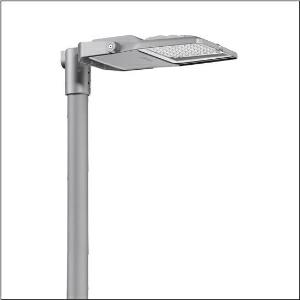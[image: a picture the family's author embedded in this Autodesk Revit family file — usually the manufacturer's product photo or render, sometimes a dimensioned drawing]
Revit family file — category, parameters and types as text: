
# Revit family: floodlight_fl_21_mini___pl43_5xa7776d2a3a_6ee6
name_source: partatom
category: Lighting Fixtures
units: mm (PartAtom-declared; Revit-internal decimal feet)

## family parameters
Cut with Voids When Loaded = No
Host = Face
Light Source = No
Part Type = Normal
Room Calculation Point = No
Round Connector Dimension = Use Diameter
Shared = No

## types (1)
- --- (1 x LED, 18300 lm, 142.9 W, 3000K)
    Apparent Load = 143 VA
    CIE Flux Codes = 27 78 99 100 100
    Color Rendering = 70
    Color Temperature = 3000K
    Default Elevation = 1800 mm
    Description = Floodlight FL 21 mini, floodlight, primary light control with lens, of PMMA, primary optical cover: protective disc, of toughened safety glass, transparent, light distribution: PL43, light emission: direct distribution, installation type: surface-mounted, LED, High Power LED, rated luminous flux: 18.300lm, luminous efficacy: 128lm/W, light colour: 730, colour temperature: 3000K, control: flexible luminous flux parameterisation, time-dependent luminous flux control, constant luminous flux control, overheat protection, pre-setting: logarithmic dimming characteristic, with terminal, 6-pole, mains connection: 220..240V, AC, 50/60Hz, start of lifetime: 143W, end of service life: 151W, reduction: 63W, luminaire housing, of diecast aluminium, powder-coated, Siteco® metallic grey (DB 702S), corrosivity category C5 mid according to DIN EN ISO 12944, sealing non-destructively replaceable, please order mast flange separately, mast bracket, of steel, galvanised, powder-coated, Siteco® metallic grey (DB 702S), Smart Interface below and above, protection rating (complete): IP66, insulation class (complete): insulation class II (safety insulation), certification: CE, ENEC, VDE, protection symbol: D, impact resistance: IK08, permissible operating ambient temperature: -40..+40°C, permissible operating ambient temperature for outdoor applications: -40..+50°C, standard: DIN EN 12944, LABS conformity tested according to VDMA 24364:2018-05, packaging unit: 1 piece

Light Distribution: PL43
    Height = 70 mm
    Lamp = 1 x LED
    Lamp Light Flux = 18300 lm
    Lamp Power = 142.9 W
    Lamp count = 1
    Length = 485 mm
    Luminous efficacy = 128 lm/W
    Manufacturer = Siteco
    ModVariant = No
    Model = 5XA7776D2A3A
    Number of Poles = 1
    OnlyDefault = Yes
    Power Factor = 1
    Product Name = Floodlight FL 21 mini | PL43
    Product group = floodlight | pylon annexe
    ProductGroupID = 6200
    Protection Class = Protection class II
    Protection Degree = IP 66
    RLX_Detail_Level = 1
    RLX_Emergency_Light_Flux = 0 lm
    RLX_Emergency_Type = 0
    RLX_Emergency_Type_DB = No
    RlxData = <blob elided: 101181 chars, md5=948c9c48>
    Socket = socket
    Standby Power = 0 W
    System Light Flux = 18300 lm
    System Power = 143 W
    Type Comments = factory setting: luminous flux: 100 % | dim-lin: 254 | 730 mA
    Type Image = l_1007125.jpg
    URL = http://relux.com
    VarID = @adj_131285
    Voltage = 0 V
    Weight = 0.00 kg
    Width = 337 mm

## geometry (parser evidence)
native form markers: Blend x4, Sweep x11
no freeform markers — native parametric forms only
